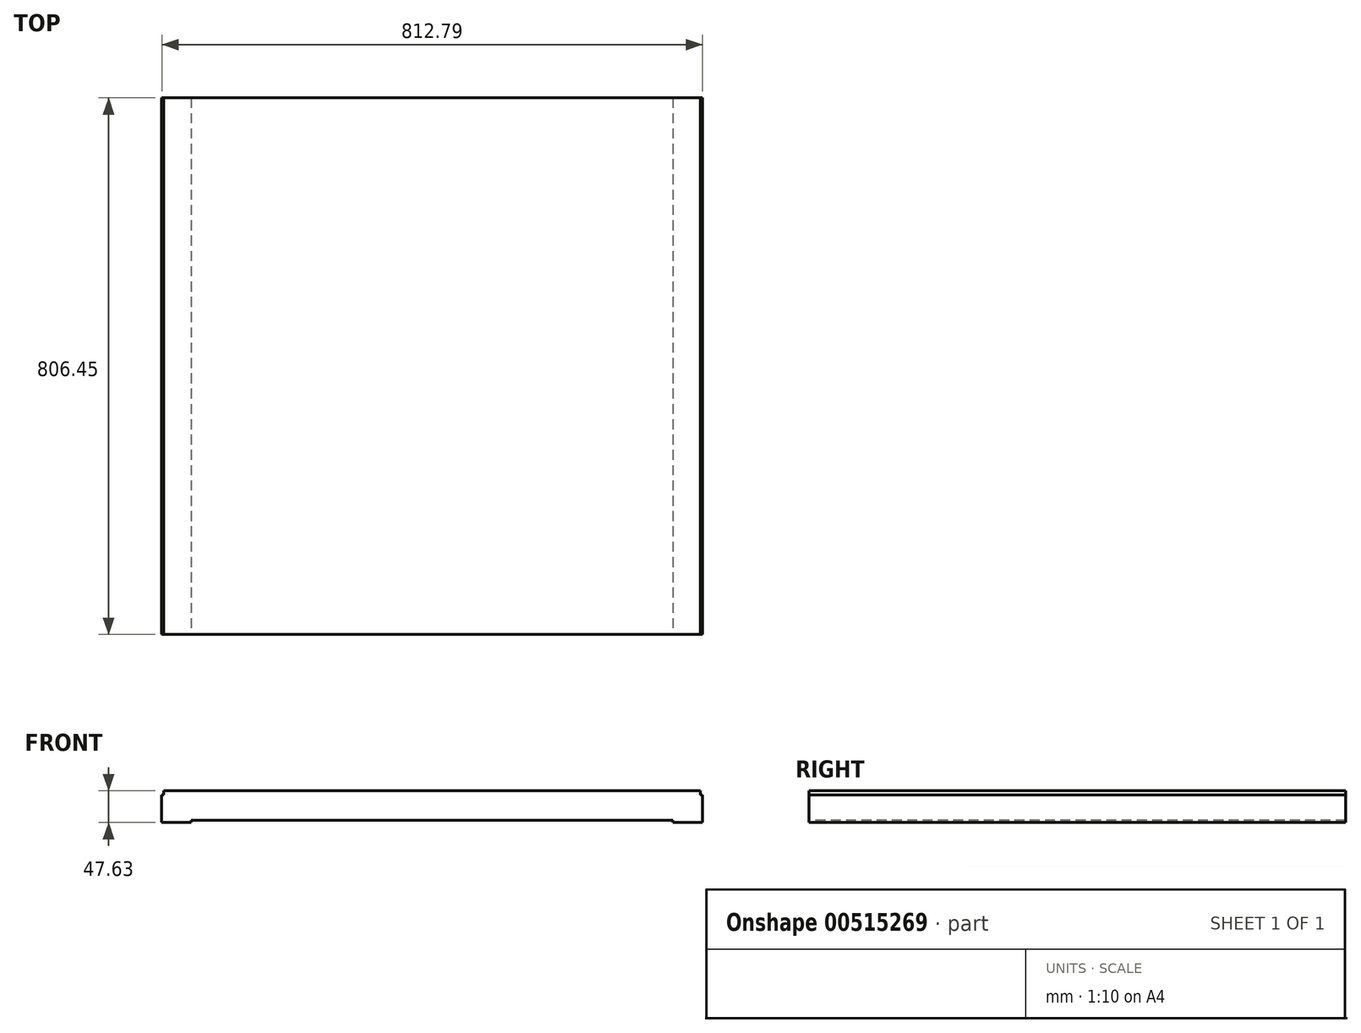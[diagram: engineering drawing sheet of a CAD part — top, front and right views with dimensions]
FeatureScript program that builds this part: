
annotation { "Feature Type Name" : "Feature", "Feature Type Description" : "" }
export const myFeature = defineFeature(function(context is Context, id is Id, definition is map)
    precondition{}
    {
        {
            var Q0;
            Q0=qCreatedBy(makeId("Front.planeOp"),FACE);
            var sketch = newSketch(context, id + "F0", { "sketchPlane" : qUnion([Q0])});
            skLineSegment(sketch, "E0.bottom", {"start": v(0, 0) * mm, "end": v(806.45, 0) * mm});
            skLineSegment(sketch, "E0.top", {"start": v(0, 44.45) * mm, "end": v(806.45, 44.45) * mm});
            skLineSegment(sketch, "E0.left", {"start": v(0, 0) * mm, "end": v(0, 44.45) * mm});
            skLineSegment(sketch, "E0.right", {"start": v(806.45, 0) * mm, "end": v(806.45, 44.45) * mm});
            skSolve(sketch);
        }
        {
            var Q0;
            Q0=makeQuery(id+"F0.imprint","IMPRINT",FACE,{"disambiguationData":[TD([[makeQuery(id+"F0.imprint","IMPRINT",EDGE,{"derivedFrom":sQuery(id+"F0.wireOp",EDGE,"E0.bottom")}),1.0]])]});
            extrude(context, id + "F1", {"entities" : qUnion([Q0]), "oppositeDirection" : true, "depth" : 806.45 * mm, "offsetDistance" : 25.4 * mm});
        }
        {
            var Q0;
            Q0=qCreatedBy(makeId("Front.planeOp"),FACE);
            var sketch = newSketch(context, id + "F2", { "sketchPlane" : qUnion([Q0])});
            skLineSegment(sketch, "E1", {"start": v(0, -3.18) * mm, "end": v(41.28, -3.18) * mm});
            skLineSegment(sketch, "E2", {"start": v(0, -3.18) * mm, "end": v(-3.18, -3.18) * mm});
            skLineSegment(sketch, "E3", {"start": v(-3.18, -3.18) * mm, "end": v(-3.18, 38.1) * mm});
            skLineSegment(sketch, "E4", {"start": v(-3.18, 38.1) * mm, "end": v(0, 38.1) * mm});
            skLineSegment(sketch, "E5", {"start": v(0, 38.1) * mm, "end": v(0, 0) * mm});
            skLineSegment(sketch, "E6", {"start": v(41.28, 0) * mm, "end": v(41.28, -3.18) * mm});
            skLineSegment(sketch, "E7", {"start": v(0, 0) * mm, "end": v(41.28, 0) * mm});
            skLineSegment(sketch, "E8", {"start": v(403.23, 0) * mm, "end": v(403.23, 44.45) * mm});
            skLineSegment(sketch, "E9.MirrorCS", {"start": v(806.45, -3.18) * mm, "end": v(809.62, -3.18) * mm});
            skLineSegment(sketch, "E10.MirrorCS", {"start": v(765.18, 0) * mm, "end": v(765.18, -3.18) * mm});
            skLineSegment(sketch, "E11.MirrorCS", {"start": v(809.62, 38.1) * mm, "end": v(806.45, 38.1) * mm});
            skLineSegment(sketch, "E12.MirrorCS", {"start": v(806.45, -3.18) * mm, "end": v(765.18, -3.18) * mm});
            skLineSegment(sketch, "E13.MirrorCS", {"start": v(806.45, 38.1) * mm, "end": v(806.45, 0) * mm});
            skLineSegment(sketch, "E14.MirrorCS", {"start": v(809.63, -3.18) * mm, "end": v(809.63, 38.1) * mm});
            skLineSegment(sketch, "E15.MirrorCS", {"start": v(806.45, 0) * mm, "end": v(765.18, 0) * mm});
            skSolve(sketch);
        }
        {
            var Q0;
            Q0=makeQuery(id+"F2.imprint","IMPRINT",FACE,{"disambiguationData":[TD([[makeQuery(id+"F2.imprint","IMPRINT",EDGE,{"derivedFrom":sQuery(id+"F2.wireOp",EDGE,"E1")}),1.0]])]});
            var Q1;
            Q1=makeQuery(id+"F2.imprint","IMPRINT",FACE,{"disambiguationData":[TD([[makeQuery(id+"F2.imprint","IMPRINT",EDGE,{"derivedFrom":sQuery(id+"F2.wireOp",EDGE,"E9.MirrorCS")}),1.0]])]});
            extrude(context, id + "F3", {"entities" : qUnion([Q0, Q1]), "operationType" : NewBodyOperationType.ADD, "oppositeDirection" : true, "depth" : 806.45 * mm, "offsetDistance" : 25.4 * mm});
        }
    });
